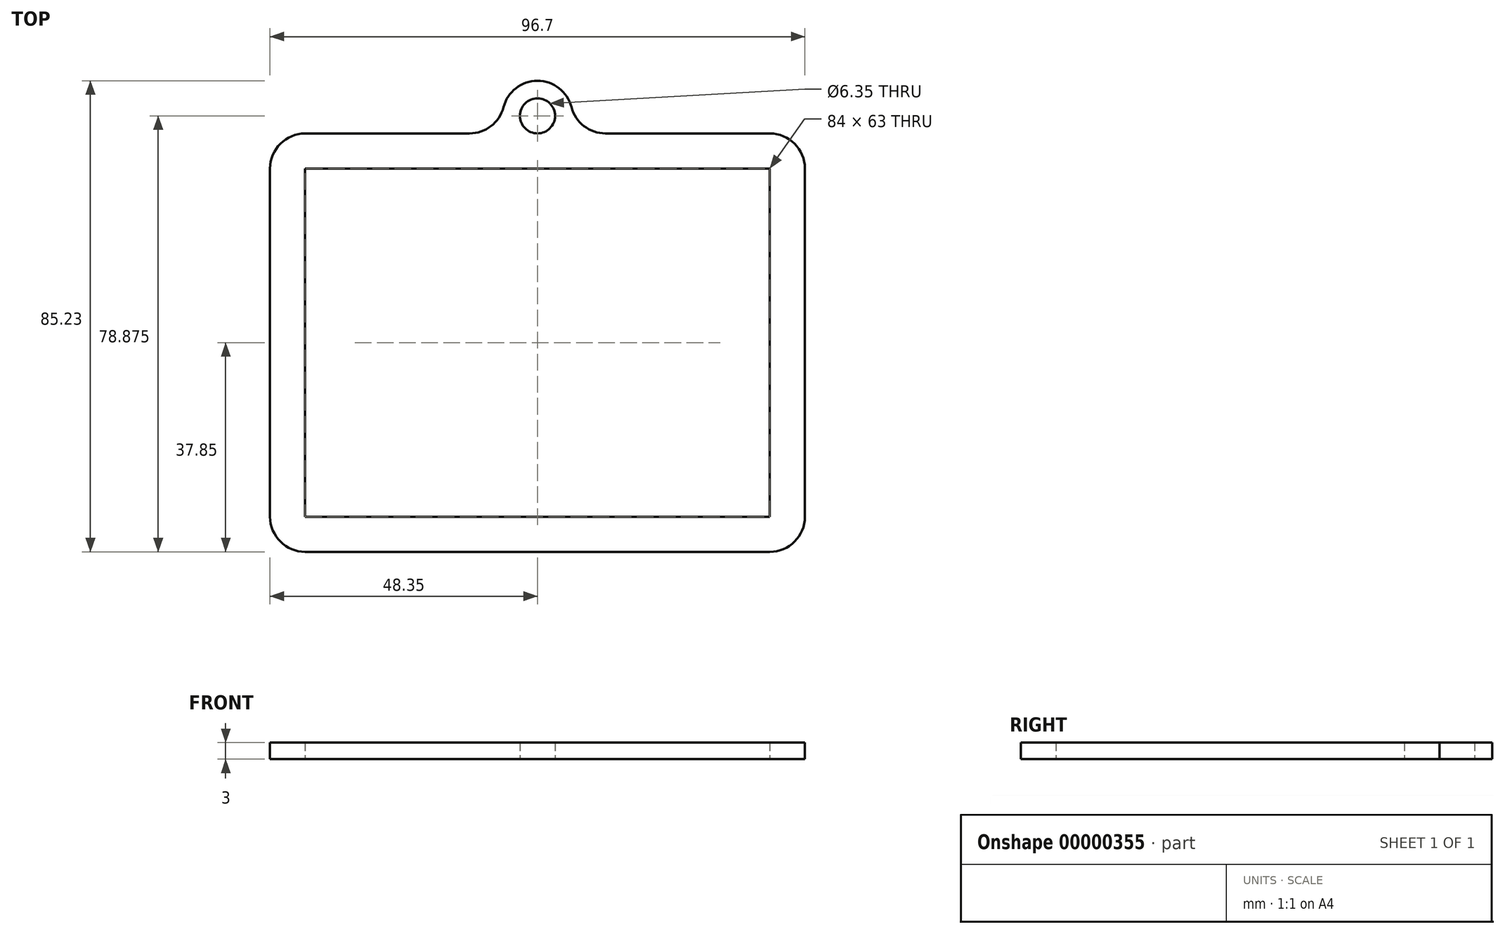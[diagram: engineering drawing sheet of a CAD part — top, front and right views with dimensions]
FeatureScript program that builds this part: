
annotation { "Feature Type Name" : "Feature", "Feature Type Description" : "" }
export const myFeature = defineFeature(function(context is Context, id is Id, definition is map)
    precondition{}
    {
        {
            var Q0;
            Q0=qCreatedBy(makeId("Top.planeOp"),FACE);
            var sketch = newSketch(context, id + "F0", { "sketchPlane" : qUnion([Q0])});
            skLineSegment(sketch, "E0.rect.bottom", {"start": v(-42, 31.5) * mm, "end": v(42, 31.5) * mm});
            skLineSegment(sketch, "E0.rect.top", {"start": v(-42, -31.5) * mm, "end": v(42, -31.5) * mm});
            skLineSegment(sketch, "E0.rect.left", {"start": v(-42, 31.5) * mm, "end": v(-42, -31.5) * mm});
            skLineSegment(sketch, "E0.rect.right", {"start": v(42, 31.5) * mm, "end": v(42, -31.5) * mm});
            skPoint(sketch, "E0.rect.middle", {"position": v(0, 0) * mm});
            skLineSegment(sketch, "E1.0", {"start": v(-42, 37.85) * mm, "end": v(-12.3, 37.85) * mm});
            skLineSegment(sketch, "E1.1", {"start": v(-48.35, 31.5) * mm, "end": v(-48.35, -31.5) * mm});
            skLineSegment(sketch, "E1.2", {"start": v(-42, -37.85) * mm, "end": v(42, -37.85) * mm});
            skLineSegment(sketch, "E1.3", {"start": v(48.35, 31.5) * mm, "end": v(48.35, -31.5) * mm});
            skPoint(sketch, "E2.visualSharp", {"position": v(-48.35, 37.85) * mm});
            skArc(sketch, "E2.filletArc", {"start": v(-42, 37.85) * mm, "mid": v(-46.5, 36) * mm, "end": v(-48.35, 31.5) * mm});
            skPoint(sketch, "E3.visualSharp", {"position": v(-48.35, -37.85) * mm});
            skArc(sketch, "E3.filletArc", {"start": v(-48.35, -31.5) * mm, "mid": v(-46.5, -36) * mm, "end": v(-42, -37.85) * mm});
            skPoint(sketch, "E4.visualSharp", {"position": v(48.35, -37.85) * mm});
            skArc(sketch, "E4.filletArc", {"start": v(42, -37.85) * mm, "mid": v(46.5, -36) * mm, "end": v(48.35, -31.5) * mm});
            skPoint(sketch, "E5.visualSharp", {"position": v(48.35, 37.85) * mm});
            skArc(sketch, "E5.filletArc", {"start": v(48.35, 31.5) * mm, "mid": v(46.5, 36) * mm, "end": v(42, 37.85) * mm});
            skCircle(sketch, "E6", {"center": v(0, 41.02) * mm, "radius": 3.18 * mm});
            skArc(sketch, "E7", {"start": v(6.15, 42.61) * mm, "mid": v(0, 47.38) * mm, "end": v(-6.15, 42.61) * mm});
            skLineSegment(sketch, "E8.trimOffspring", {"start": v(12.3, 37.85) * mm, "end": v(42, 37.85) * mm});
            skPoint(sketch, "E9.visualSharp", {"position": v(-5.5, 37.85) * mm});
            skArc(sketch, "E9.filletArc", {"start": v(-12.3, 37.85) * mm, "mid": v(-8.4, 39.18) * mm, "end": v(-6.15, 42.61) * mm});
            skPoint(sketch, "E10.visualSharp", {"position": v(5.5, 37.85) * mm});
            skArc(sketch, "E10.filletArc", {"start": v(6.15, 42.61) * mm, "mid": v(8.4, 39.18) * mm, "end": v(12.3, 37.85) * mm});
            skSolve(sketch);
        }
        {
            var Q0;
            Q0=makeQuery(id+"F0.imprint","IMPRINT",FACE,{"disambiguationData":[TD([[makeQuery(id+"F0.imprint","IMPRINT",EDGE,{"derivedFrom":sQuery(id+"F0.wireOp",EDGE,"E0.rect.bottom")}),1.0]])]});
            extrude(context, id + "F1", {"entities" : qUnion([Q0]), "depth" : 3 * mm});
        }
    });
